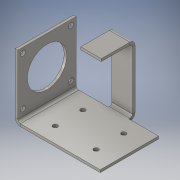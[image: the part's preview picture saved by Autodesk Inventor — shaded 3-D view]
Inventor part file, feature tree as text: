
AUTODESK INVENTOR PART (.ipt)
format: ipt  version: 2016 (Build 200138000, 138)  size: 250,880 bytes
history: native  units: in
note: dims shown in document units (in); Inventor stores cm internally (conversion verified against a paired STEP export)
features: sheet_metal_op x10, sketch x7, other x7, extrude x1
ambient origin geometry x8: Origin, YZ Plane, XZ Plane, XY Plane, X Axis, Y Axis, Z Axis, Center Point
bodies: Solid1 (feature_tree)
feature tree (25):
  sheet_metal_op  "Face1"
  sheet_metal_op  "Flange1"
  extrude  "Extrusion1"  Depth=2.2441in
  sheet_metal_op  "Flange2"
  sheet_metal_op  "Flange3"
  sketch  "Sketch1"  dims[d0=3.0709in d1=2.2441in]
  other  "Plate1"
  sketch  "Sketch2"  dims[d2=0.0984in]
  other  "Plate2"
  sheet_metal_op  "Bend1"
  sheet_metal_op  "Corner1"
  sketch  "Sketch3"  dims[d3=0.0984in]
  sketch  "Sketch4"  dims[d4=0.0492in]
  sketch  "Sketch5"  dims[d5=0.1969in]
  other  "Plate3"
  sheet_metal_op  "Bend2"
  sheet_metal_op  "Corner2"
  sketch  "Sketch6"  dims[d6=0.0984in]
  other  "Plate4"
  sheet_metal_op  "Bend3"
  sheet_metal_op  "Corner3"
  sketch  "Sketch7"  dims[d7=2.5in d8=90.0deg d9=0.0984in d10=0.3937in d11=0.0984in d12=0.0984in d13=2.2441in d14=1.5157in d15=0.1969in d16=0.1969in d17=0.1969in d18=0.1969in d19=0.1969in d20=0.1969in d21=0.1969in d22=0.1969in d23=0.1969in d24=0.1969in d25=0.1969in d26=0.1969in d27=0.0984in d28=0.0in d29=0.3937in d30=0.7874in d31=0.0394in d32=0.0in d33=0.0984in d34=0.0492in d35=0.1969in d36=0.0984in d37=2.4409in d38=90.0deg d39=0.0984in d40=0.3937in d41=0.0984in d42=0.0984in d43=0.0984in d44=0.0492in d45=0.1969in d46=0.0984in d47=1.2992in d48=90.0deg d49=0.0984in d50=0.3937in d51=0.0984in d52=0.0984in d53=0.5906in d54=0.7874in d55=0.7874in d56=0.1772in d57=0.1772in d58=1.063in d59=0.7874in d60=0.7874in d61=0.1772in d62=0.1772in d63=0.0984in d64=0.0in]
  other  "Cut1"
  other  "Cut2"
  other  "Definition1"
